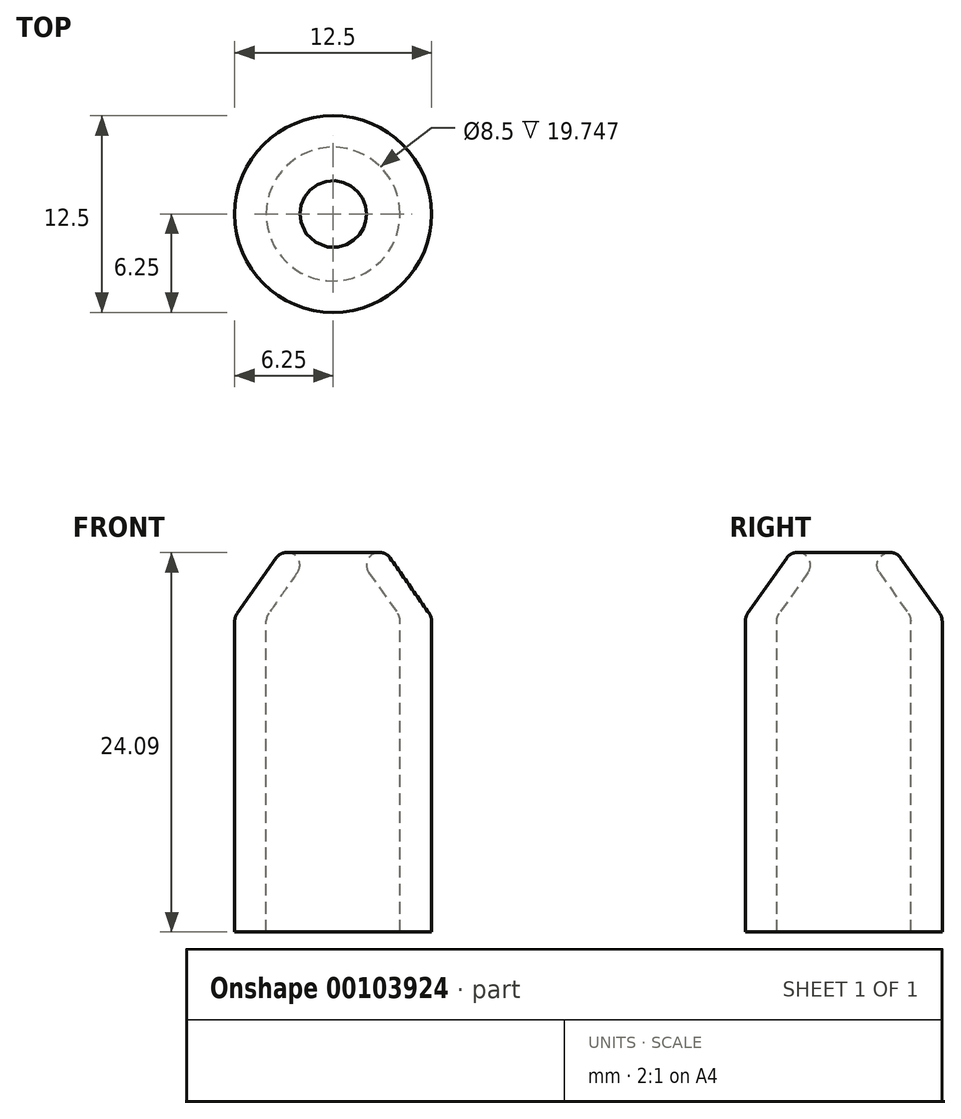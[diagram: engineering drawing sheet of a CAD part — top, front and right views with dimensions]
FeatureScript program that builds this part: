
annotation { "Feature Type Name" : "Feature", "Feature Type Description" : "" }
export const myFeature = defineFeature(function(context is Context, id is Id, definition is map)
    precondition{}
    {
        {
            var Q0;
            Q0=qCreatedBy(makeId("Front.planeOp"),FACE);
            var sketch = newSketch(context, id + "F0", { "sketchPlane" : qUnion([Q0])});
            skLineSegment(sketch, "E0", {"start": v(-1.38, 6.92) * mm, "end": v(-3.38, 6.92) * mm});
            skLineSegment(sketch, "E1", {"start": v(-3.38, 6.92) * mm, "end": v(-6.25, 2.83) * mm});
            skLineSegment(sketch, "E2", {"start": v(-6.25, 2.83) * mm, "end": v(-6.25, -17.17) * mm});
            skLineSegment(sketch, "E3", {"start": v(-6.25, -17.17) * mm, "end": v(-4.25, -17.17) * mm});
            skLineSegment(sketch, "E4", {"start": v(-4.25, -17.17) * mm, "end": v(-4.25, 2.83) * mm});
            skLineSegment(sketch, "E5", {"start": v(-4.25, 2.83) * mm, "end": v(-1.38, 6.92) * mm});
            skLineSegment(sketch, "E6", {"start": v(0, 13.36) * mm, "end": v(0, -16.07) * mm, "construction": true});
            skSolve(sketch);
        }
        {
            var Q0;
            Q0=makeQuery(id+"F0.imprint","IMPRINT",FACE,{"disambiguationData":[TD([[makeQuery(id+"F0.imprint","IMPRINT",EDGE,{"derivedFrom":sQuery(id+"F0.wireOp",EDGE,"E0")}),1.0]])]});
            var Q1;
            Q1=sQuery(id+"F0.wireOp",EDGE,"E6");
            revolve(context, id + "F1", {"entities" : qUnion([Q0]), "axis" : qUnion([Q1]), "revolveType" : RevolveType.FULL});
        }
        {
            var Q0;
            Q0=makeQuery(id+"F1.opRevolve","SWEPT_EDGE",EDGE,{"disambiguationData":[OSD([sQuery(id+"F0.wireOp",EDGE,"E0"),sQuery(id+"F0.wireOp",EDGE,"E5")])]});
            var Q1;
            Q1=makeQuery(id+"F1.opRevolve","SWEPT_EDGE",EDGE,{"disambiguationData":[OSD([sQuery(id+"F0.wireOp",EDGE,"E0"),sQuery(id+"F0.wireOp",EDGE,"E1")])]});
            var Q2;
            Q2=makeQuery(id+"F1.opRevolve","SWEPT_EDGE",EDGE,{"disambiguationData":[OSD([sQuery(id+"F0.wireOp",EDGE,"E1"),sQuery(id+"F0.wireOp",EDGE,"E2")])]});
            var Q3;
            Q3=makeQuery(id+"F1.opRevolve","SWEPT_FACE",FACE,{"disambiguationData":[OSD([sQuery(id+"F0.wireOp",EDGE,"E5")])]});
            fillet(context, id + "F2", {"entities" : qUnion([Q0, Q1, Q2, Q3]), "radius" : .8 * mm, "tangentPropagation" : true, "allowEdgeOverflow" : false});
        }
    });
